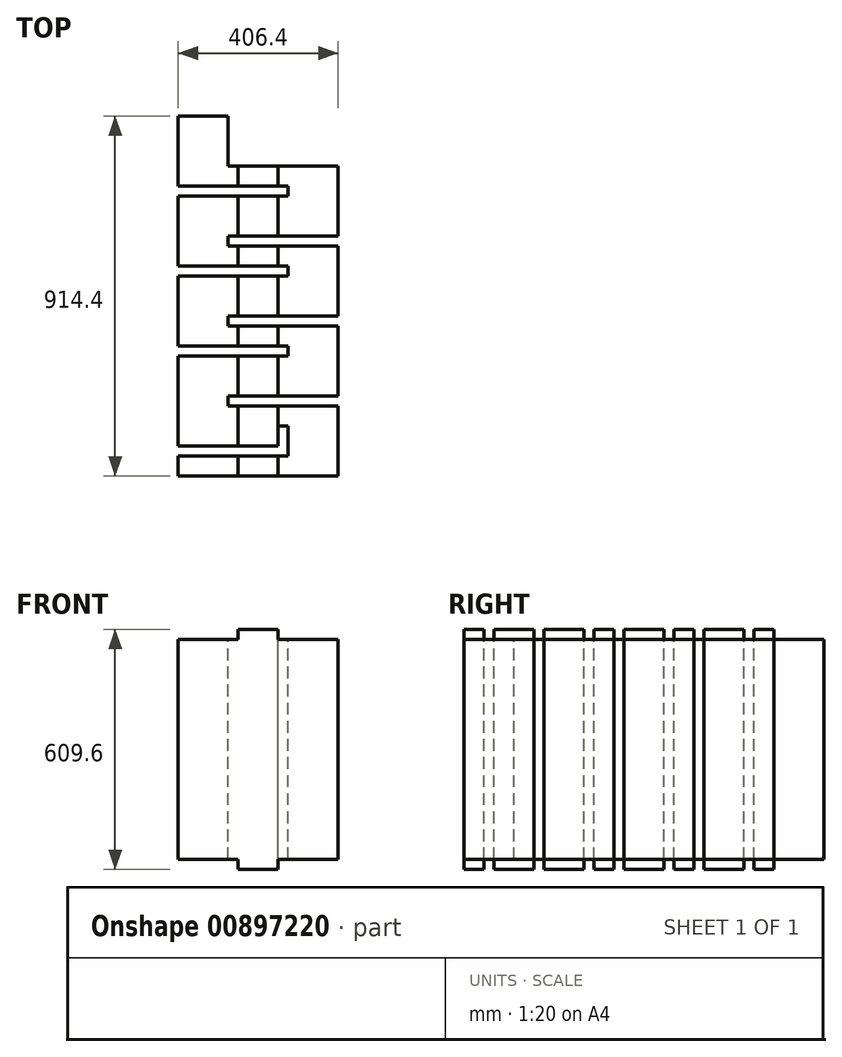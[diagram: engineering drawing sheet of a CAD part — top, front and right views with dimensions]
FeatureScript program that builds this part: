
annotation { "Feature Type Name" : "Feature", "Feature Type Description" : "" }
export const myFeature = defineFeature(function(context is Context, id is Id, definition is map)
    precondition{}
    {
        {
            var Q0;
            Q0=qCreatedBy(makeId("Top.planeOp"),FACE);
            var sketch = newSketch(context, id + "F0", { "sketchPlane" : qUnion([Q0])});
            skLineSegment(sketch, "E0", {"start": v(0, 0) * mm, "end": v(127, 0) * mm});
            skLineSegment(sketch, "E1", {"start": v(127, 0) * mm, "end": v(127, -127) * mm});
            skLineSegment(sketch, "E2", {"start": v(127, -127) * mm, "end": v(406.4, -127) * mm});
            skLineSegment(sketch, "E3", {"start": v(406.4, -127) * mm, "end": v(406.4, -304.8) * mm});
            skLineSegment(sketch, "E4", {"start": v(406.4, -304.8) * mm, "end": v(127, -304.8) * mm});
            skLineSegment(sketch, "E5", {"start": v(127, -304.8) * mm, "end": v(127, -330.2) * mm});
            skLineSegment(sketch, "E6", {"start": v(127, -330.2) * mm, "end": v(406.4, -330.2) * mm});
            skLineSegment(sketch, "E7", {"start": v(406.4, -330.2) * mm, "end": v(406.4, -508) * mm});
            skLineSegment(sketch, "E8", {"start": v(406.4, -508) * mm, "end": v(127, -508) * mm});
            skLineSegment(sketch, "E9", {"start": v(127, -508) * mm, "end": v(127, -533.4) * mm});
            skLineSegment(sketch, "E10", {"start": v(127, -533.4) * mm, "end": v(406.4, -533.4) * mm});
            skLineSegment(sketch, "E11", {"start": v(406.4, -533.4) * mm, "end": v(406.4, -711.2) * mm});
            skLineSegment(sketch, "E12", {"start": v(406.4, -711.2) * mm, "end": v(127, -711.2) * mm});
            skLineSegment(sketch, "E13", {"start": v(127, -711.2) * mm, "end": v(127, -736.6) * mm});
            skLineSegment(sketch, "E14", {"start": v(127, -736.6) * mm, "end": v(406.4, -736.6) * mm});
            skLineSegment(sketch, "E15", {"start": v(406.4, -736.6) * mm, "end": v(406.4, -914.4) * mm});
            skLineSegment(sketch, "E16", {"start": v(406.4, -914.4) * mm, "end": v(279.4, -914.4) * mm});
            skLineSegment(sketch, "E17", {"start": v(279.4, -914.4) * mm, "end": v(279.4, -787.4) * mm});
            skLineSegment(sketch, "E18", {"start": v(279.4, -787.4) * mm, "end": v(0, -787.4) * mm});
            skLineSegment(sketch, "E19", {"start": v(0, -787.4) * mm, "end": v(0, -609.6) * mm});
            skLineSegment(sketch, "E20", {"start": v(0, -609.6) * mm, "end": v(279.4, -609.6) * mm});
            skLineSegment(sketch, "E21", {"start": v(279.4, -609.6) * mm, "end": v(279.4, -584.2) * mm});
            skLineSegment(sketch, "E22", {"start": v(279.4, -584.2) * mm, "end": v(0, -584.2) * mm});
            skLineSegment(sketch, "E23", {"start": v(0, -584.2) * mm, "end": v(0, -406.4) * mm});
            skLineSegment(sketch, "E24", {"start": v(0, -406.4) * mm, "end": v(279.4, -406.4) * mm});
            skLineSegment(sketch, "E25", {"start": v(279.4, -406.4) * mm, "end": v(279.4, -381) * mm});
            skLineSegment(sketch, "E26", {"start": v(279.4, -381) * mm, "end": v(0, -381) * mm});
            skLineSegment(sketch, "E27", {"start": v(0, -381) * mm, "end": v(0, -203.2) * mm});
            skLineSegment(sketch, "E28", {"start": v(0, -203.2) * mm, "end": v(279.4, -203.2) * mm});
            skLineSegment(sketch, "E29", {"start": v(279.4, -203.2) * mm, "end": v(279.4, -177.8) * mm});
            skLineSegment(sketch, "E30", {"start": v(279.4, -177.8) * mm, "end": v(0, -177.8) * mm});
            skLineSegment(sketch, "E31", {"start": v(0, -177.8) * mm, "end": v(0, 0) * mm});
            skLineSegment(sketch, "E32.bottom", {"start": v(0, -787.4) * mm, "end": v(254, -787.4) * mm});
            skLineSegment(sketch, "E32.top", {"start": v(0, -838.2) * mm, "end": v(254, -838.2) * mm});
            skLineSegment(sketch, "E32.left", {"start": v(0, -787.4) * mm, "end": v(0, -838.2) * mm});
            skLineSegment(sketch, "E32.right", {"start": v(254, -787.4) * mm, "end": v(254, -838.2) * mm});
            skLineSegment(sketch, "E33.bottom", {"start": v(279.4, -914.4) * mm, "end": v(0, -914.4) * mm});
            skLineSegment(sketch, "E33.top", {"start": v(279.4, -863.6) * mm, "end": v(0, -863.6) * mm});
            skLineSegment(sketch, "E33.left", {"start": v(279.4, -914.4) * mm, "end": v(279.4, -863.6) * mm});
            skLineSegment(sketch, "E33.right", {"start": v(0, -914.4) * mm, "end": v(0, -863.6) * mm});
            skSolve(sketch);
        }
        {
            var Q0;
            Q0 = qSketchRegion(id + "F0", true);
            extrude(context, id + "F1", {"entities" : qUnion([Q0]), "oppositeDirection" : true, "depth" : 609.6 * mm, "offsetDistance" : 25.4 * mm});
        }
        {
            var Q0;
            Q0=makeQuery(id+"F1.opExtrude","SWEPT_FACE",FACE,{"disambiguationData":[OSD([sQuery(id+"F0.wireOp",EDGE,"E16")])]});
            var sketch = newSketch(context, id + "F2", { "sketchPlane" : qUnion([Q0])});
            skLineSegment(sketch, "E34.bottom", {"start": v(0, 0) * mm, "end": v(152.4, 0) * mm});
            skLineSegment(sketch, "E34.top", {"start": v(0, -25.4) * mm, "end": v(152.4, -25.4) * mm});
            skLineSegment(sketch, "E34.left", {"start": v(0, 0) * mm, "end": v(0, -25.4) * mm});
            skLineSegment(sketch, "E34.right", {"start": v(152.4, 0) * mm, "end": v(152.4, -25.4) * mm});
            skLineSegment(sketch, "E35.bottom", {"start": v(406.4, 0) * mm, "end": v(254, 0) * mm});
            skLineSegment(sketch, "E35.top", {"start": v(406.4, -25.4) * mm, "end": v(254, -25.4) * mm});
            skLineSegment(sketch, "E35.left", {"start": v(406.4, 0) * mm, "end": v(406.4, -25.4) * mm});
            skLineSegment(sketch, "E35.right", {"start": v(254, 0) * mm, "end": v(254, -25.4) * mm});
            skLineSegment(sketch, "E36", {"start": v(406.4, -304.8) * mm, "end": v(-85.57, -304.8) * mm, "construction": true});
            skLineSegment(sketch, "E37.MirrorCS", {"start": v(0, -609.6) * mm, "end": v(0, -584.2) * mm});
            skLineSegment(sketch, "E38.MirrorCS", {"start": v(0, -609.6) * mm, "end": v(152.4, -609.6) * mm});
            skLineSegment(sketch, "E39.MirrorCS", {"start": v(152.4, -609.6) * mm, "end": v(152.4, -584.2) * mm});
            skLineSegment(sketch, "E40.MirrorCS", {"start": v(254, -609.6) * mm, "end": v(254, -584.2) * mm});
            skLineSegment(sketch, "E41.MirrorCS", {"start": v(0, -584.2) * mm, "end": v(152.4, -584.2) * mm});
            skLineSegment(sketch, "E42.MirrorCS", {"start": v(406.4, -609.6) * mm, "end": v(254, -609.6) * mm});
            skLineSegment(sketch, "E43.MirrorCS", {"start": v(406.4, -584.2) * mm, "end": v(254, -584.2) * mm});
            skLineSegment(sketch, "E44.MirrorCS", {"start": v(406.4, -609.6) * mm, "end": v(406.4, -584.2) * mm});
            skSolve(sketch);
        }
        {
            var Q0;
            Q0 = qSketchRegion(id + "F2", true);
            extrude(context, id + "F3", {"entities" : qUnion([Q0]), "operationType" : NewBodyOperationType.REMOVE, "endBound" : BoundingType.THROUGH_ALL, "oppositeDirection" : true, "depth" : 25.4 * mm, "offsetDistance" : 25.4 * mm});
        }
    });
